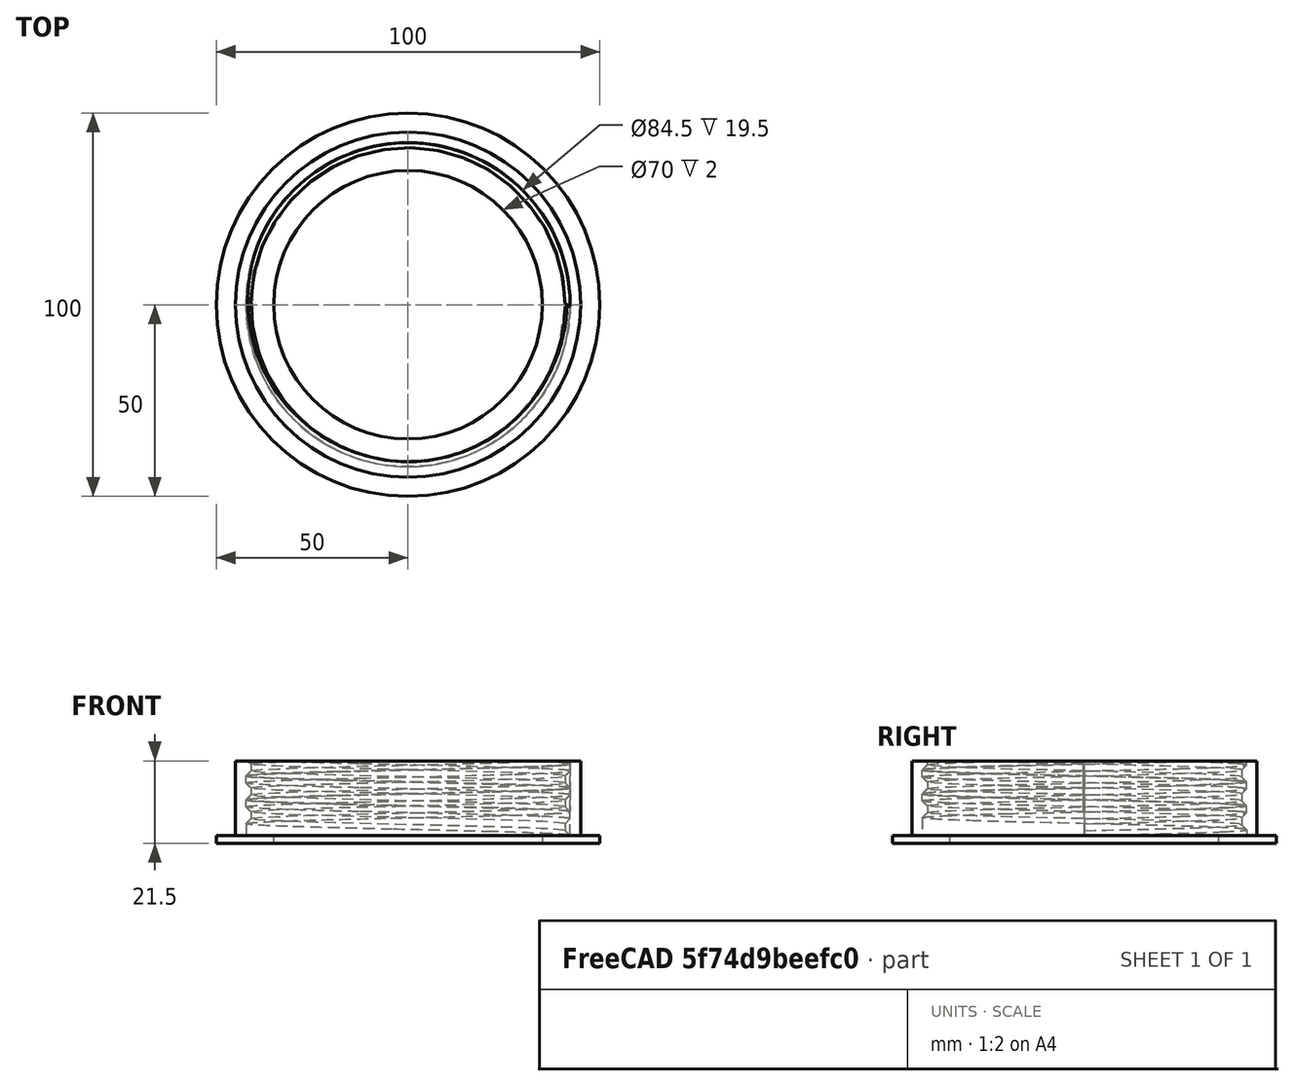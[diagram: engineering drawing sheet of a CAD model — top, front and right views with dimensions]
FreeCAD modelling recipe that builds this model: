
FCSTD DOCUMENT  (FreeCAD 0.19R)
Label: Vis
License: All rights reserved
LicenseURL: http://en.wikipedia.org/wiki/All_rights_reserved
objects: Sketcher::SketchObject×5, PartDesign::Pad×2, Part::Helix×1, PartDesign::ShapeBinder×1, PartDesign::AdditivePipe×1, PartDesign::LinearPattern×1, PartDesign::Pocket×1, PartDesign::Body×1, Mesh::Feature×1
note: 17 computed .brp shape members not serialized (recipe doc carries the construction recipe); baked Part::Feature solids carry a one-line shape summary decoded from their .brp

FEATURE [Sketcher::SketchObject] Sketch
  FullyConstrained = true
  MapMode = 5
  Support = -> [XY_Plane]
FEATURE [Part::Helix] Helix
  Angle = 0
  AttacherType = Attacher::AttachEngine3D
  Height = 6.22
  LocalCoord = 0
  Pitch = 6.23
  Radius = 40.5
  Style = 1
FEATURE [Sketcher::SketchObject] Sketch001
  FullyConstrained = true
  MapMode = 5
  Support = -> [XY_Plane]
  sketch-geometry (2):
    g0: Circle CenterX=0 CenterY=0 CenterZ=0 NormalX=0 NormalY=0 NormalZ=1 AngleXU=0 Radius=42.25
    g1: Circle CenterX=0 CenterY=0 CenterZ=0 NormalX=0 NormalY=0 NormalZ=1 AngleXU=0 Radius=45
  constraints (4):
    c: Coincident(g0,g-1)
    c: Coincident(g1,g0)
    c: Radius(g0) = 42.25
    c: Radius(g1) = 45
FEATURE [PartDesign::Pad] Pad
  Direction = (1,1,1)
  Length = 20
  Length2 = 100
  Profile = -> Sketch001
  Type = 0
FEATURE [Sketcher::SketchObject] Sketch002  label="Profile"
  FullyConstrained = true
  MapMode = 5
  Placement = pos=(0,0,0) rot=(1,0,0;1.5708rad)
  Support = -> [XZ_Plane]
  sketch-geometry (7):
    g0: LineSegment StartX=42.25 StartY=4.40427 StartZ=0 EndX=40.9557 EndY=3.11 EndZ=0
    g1: LineSegment StartX=40.9557 StartY=3.11 StartZ=0 EndX=40.9557 EndY=1.29427 EndZ=0
    g2: LineSegment StartX=40.9557 StartY=1.29427 StartZ=0 EndX=42.25 EndY=0 EndZ=0
    g3: LineSegment StartX=42.25 StartY=4.40427 StartZ=0 EndX=42.25 EndY=6.22 EndZ=0
    g4: LineSegment StartX=42.25 StartY=6.22 StartZ=0 EndX=43.25 EndY=6.22 EndZ=0
    g5: LineSegment StartX=43.25 StartY=6.22 StartZ=0 EndX=43.25 EndY=0 EndZ=0
    g6: LineSegment StartX=43.25 StartY=0 StartZ=0 EndX=42.25 EndY=0 EndZ=0
  constraints (21):
    c: Coincident(g0,g1)
    c: Vertical(g1)
    c: Coincident(g1,g2)
    c: DistanceX(g-2,g2) = 42.25
    c: PointOnObject(g2,g-1)
    c: Coincident(g0,g3)
    c: Vertical(g3)
    c: Coincident(g3,g4)
    c: Horizontal(g4)
    c: Coincident(g4,g5)
    c: PointOnObject(g5,g-1)
    c: Vertical(g5)
    c: Coincident(g5,g6)
    c: Coincident(g6,g2)
    c: DistanceX(g4,g4) = 1
    c: Equal(g3,g1)
    c: Equal(g2,g0)
    c: Angle(g2,g-1) = 0.785398
    c: Equal(g1,g3)
    c: DistanceY(g5,g5) = 6.22
    c: DistanceX(g-2,g0) = 42.25
FEATURE [PartDesign::ShapeBinder] ShapeBinder
  Support = -> [Helix]
  TraceSupport = false
FEATURE [PartDesign::AdditivePipe] AdditivePipe
  AuxilleryCurvelinear = true
  AuxillerySpineTangent = false
  BaseFeature = -> Pad
  Binormal = (0,0,0)
  Mode = 2
  Profile = -> Sketch002
  Spine = -> ShapeBinder
  SpineTangent = false
  Transformation = 0
  Transition = 0
FEATURE [PartDesign::LinearPattern] LinearPattern
  BaseFeature = -> AdditivePipe
  Direction = -> Z_Axis
  Length = 12.46
  Occurrences = 3
  Originals = -> [AdditivePipe]
FEATURE [Sketcher::SketchObject] Sketch003
  FullyConstrained = true
  MapMode = 5
  Placement = pos=(0,0,0) rot=(1,0,0;1.5708rad)
  Support = -> [XZ_Plane]
  sketch-geometry (4):
    g0: LineSegment StartX=-90 StartY=29.5 StartZ=0 EndX=90 EndY=29.5 EndZ=0
    g1: LineSegment StartX=90 StartY=29.5 StartZ=0 EndX=90 EndY=19.5 EndZ=0
    g2: LineSegment StartX=90 StartY=19.5 StartZ=0 EndX=-90 EndY=19.5 EndZ=0
    g3: LineSegment StartX=-90 StartY=19.5 StartZ=0 EndX=-90 EndY=29.5 EndZ=0
  constraints (11):
    c: Coincident(g0,g1)
    c: Coincident(g1,g2)
    c: Coincident(g2,g3)
    c: Coincident(g3,g0)
    c: Horizontal(g2)
    c: Vertical(g1)
    c: Vertical(g3)
    c: DistanceY(g-1,g1) = 19.5
    c: Symmetric(g0,g0,g-2)
    c: DistanceY(g1,g1) = 10
    c: DistanceX(g0,g0) = 180
FEATURE [PartDesign::Pocket] Pocket
  BaseFeature = -> LinearPattern
  Length = 200
  Length2 = 100
  Midplane = true
  Profile = -> Sketch003
  Type = 0
FEATURE [Sketcher::SketchObject] Sketch004
  FullyConstrained = true
  MapMode = 5
  Support = -> [XY_Plane]
  sketch-geometry (2):
    g0: Circle CenterX=0 CenterY=0 CenterZ=0 NormalX=0 NormalY=0 NormalZ=1 AngleXU=0 Radius=50
    g1: Circle CenterX=0 CenterY=0 CenterZ=0 NormalX=0 NormalY=0 NormalZ=1 AngleXU=0 Radius=35
  constraints (4):
    c: Coincident(g0,g-1)
    c: Radius(g0) = 50
    c: Coincident(g1,g0)
    c: Radius(g1) = 35
FEATURE [PartDesign::Pad] Pad001
  BaseFeature = -> Pocket
  Direction = (1,1,1)
  Length = 2
  Length2 = 100
  Profile = -> Sketch004
  Reversed = true
  Type = 0
FEATURE [PartDesign::Body] Body
  Group = -> [Sketch,Sketch001,Pad,Sketch002,ShapeBinder,AdditivePipe,LinearPattern,Sketch003,Pocket,Sketch004,Pad001]
  Origin = -> Origin
  Tip = -> Pad001
FEATURE [Mesh::Feature] Mesh  label="Body (Meshed)"
